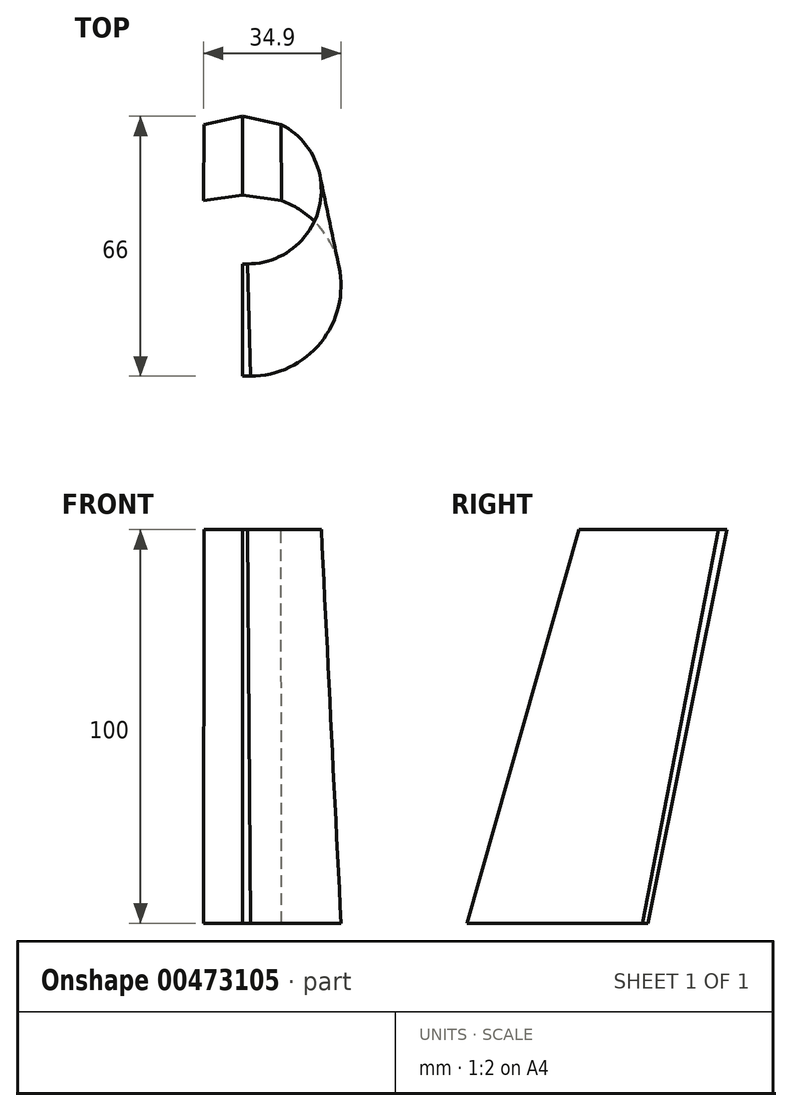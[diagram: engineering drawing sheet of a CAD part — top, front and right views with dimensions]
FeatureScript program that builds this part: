
annotation { "Feature Type Name" : "Feature", "Feature Type Description" : "" }
export const myFeature = defineFeature(function(context is Context, id is Id, definition is map)
    precondition{}
    {
        {
            var Q0;
            Q0=qCreatedBy(makeId("Top.planeOp"),FACE);
            var sketch = newSketch(context, id + "F0", { "sketchPlane" : qUnion([Q0])});
            skLineSegment(sketch, "E0.top", {"start": v(25, 0) * mm, "end": v(-25, 0) * mm, "construction": true});
            skLineSegment(sketch, "E1", {"start": v(0, 0) * mm, "end": v(9.9, -1.4) * mm});
            skLineSegment(sketch, "E2", {"start": v(0, -46) * mm, "end": v(25, -46) * mm, "construction": true});
            skLineSegment(sketch, "E3", {"start": v(25, -46) * mm, "end": v(25, 0) * mm, "construction": true});
            skArc(sketch, "E4", {"start": v(25, -46) * mm, "mid": v(2, -23) * mm, "end": v(25, 0) * mm, "construction": true});
            skLineSegment(sketch, "E5", {"start": v(0, 0) * mm, "end": v(0, -46) * mm, "construction": true});
            skLineSegment(sketch, "E6", {"start": v(2, -23) * mm, "end": v(2, -46) * mm, "construction": true});
            skArc(sketch, "E7", {"start": v(2, -46) * mm, "mid": v(24.65, -27.01) * mm, "end": v(9.9, -1.4) * mm});
            skLineSegment(sketch, "E8", {"start": v(0, -46) * mm, "end": v(2, -46) * mm});
            skLineSegment(sketch, "E9.MirrorCS", {"start": v(0, -46) * mm, "end": v(-25, -46) * mm, "construction": true});
            skLineSegment(sketch, "E10", {"start": v(-25, -46) * mm, "end": v(-17.5, -46) * mm, "construction": true});
            skLineSegment(sketch, "E11", {"start": v(-17.5, -46) * mm, "end": v(-17.5, -38.5) * mm, "construction": true});
            skArc(sketch, "E12", {"start": v(-17.5, -46) * mm, "mid": v(-22.8, -43.8) * mm, "end": v(-25, -38.5) * mm});
            skLineSegment(sketch, "E13", {"start": v(-17.5, -46) * mm, "end": v(0, -46) * mm});
            skLineSegment(sketch, "E14", {"start": v(-25, -15.9) * mm, "end": v(-15, -15.9) * mm, "construction": true});
            skArc(sketch, "E15", {"start": v(-25, -15.9) * mm, "mid": v(-23.66, -10.9) * mm, "end": v(-20, -7.23) * mm});
            skLineSegment(sketch, "E16", {"start": v(-9.9, -1.4) * mm, "end": v(-20, -7.23) * mm});
            skLineSegment(sketch, "E17.MirrorCS", {"start": v(0, 0) * mm, "end": v(-9.9, -1.4) * mm});
            skLineSegment(sketch, "E18", {"start": v(-25, -38.5) * mm, "end": v(-25, -15.9) * mm});
            skSolve(sketch);
        }
        {
            var Q0;
            Q0=qCreatedBy(makeId("Top.planeOp"),FACE);
            cPlane(context, id + "F1", {"entities" : qUnion([Q0]), "cplaneType" : CPlaneType.OFFSET, "offset" : 100 * mm, "width" : 150 * mm, "height" : 150 * mm});
        }
        {
            var Q0;
            Q0=qCreatedBy(id+"F1.planeOp",FACE);
            var sketch = newSketch(context, id + "F2", { "sketchPlane" : qUnion([Q0])});
            skLineSegment(sketch, "E19", {"start": v(0, 0) * mm, "end": v(0, 20) * mm, "construction": true});
            skLineSegment(sketch, "E20.top", {"start": v(20, 20) * mm, "end": v(-20, 20) * mm, "construction": true});
            skLineSegment(sketch, "E21", {"start": v(0, 20) * mm, "end": v(9.79, 17.94) * mm});
            skLineSegment(sketch, "E22", {"start": v(0, -17.5) * mm, "end": v(20, -17.5) * mm, "construction": true});
            skLineSegment(sketch, "E23", {"start": v(20, -17.5) * mm, "end": v(20, 20) * mm, "construction": true});
            skArc(sketch, "E24", {"start": v(20, -17.5) * mm, "mid": v(1.25, 1.25) * mm, "end": v(20, 20) * mm, "construction": true});
            skLineSegment(sketch, "E25", {"start": v(0, 20) * mm, "end": v(0, -17.5) * mm, "construction": true});
            skLineSegment(sketch, "E26", {"start": v(1.25, 1.25) * mm, "end": v(1.25, -17.5) * mm, "construction": true});
            skArc(sketch, "E27", {"start": v(1.25, -17.5) * mm, "mid": v(19.48, -3.14) * mm, "end": v(9.79, 17.94) * mm});
            skLineSegment(sketch, "E28", {"start": v(0, -17.5) * mm, "end": v(1.25, -17.5) * mm});
            skLineSegment(sketch, "E29.MirrorCS", {"start": v(0, -17.5) * mm, "end": v(-20, -17.5) * mm, "construction": true});
            skLineSegment(sketch, "E30", {"start": v(-20, -17.5) * mm, "end": v(-12.5, -17.5) * mm, "construction": true});
            skLineSegment(sketch, "E31", {"start": v(-12.5, -17.5) * mm, "end": v(-12.5, -10) * mm, "construction": true});
            skArc(sketch, "E32", {"start": v(-12.5, -17.5) * mm, "mid": v(-17.8, -15.3) * mm, "end": v(-20, -10) * mm});
            skLineSegment(sketch, "E33", {"start": v(-12.5, -17.5) * mm, "end": v(0, -17.5) * mm});
            skLineSegment(sketch, "E34", {"start": v(-20, 6.27) * mm, "end": v(-10, 6.27) * mm, "construction": true});
            skArc(sketch, "E35", {"start": v(-20, 6.27) * mm, "mid": v(-18.66, 11.27) * mm, "end": v(-15, 14.93) * mm});
            skLineSegment(sketch, "E36", {"start": v(-9.79, 17.94) * mm, "end": v(-15, 14.93) * mm});
            skLineSegment(sketch, "E37.MirrorCS", {"start": v(0, 20) * mm, "end": v(-9.79, 17.94) * mm});
            skLineSegment(sketch, "E38", {"start": v(-20, -10) * mm, "end": v(-20, 6.27) * mm});
            skSolve(sketch);
        }
        {
            var Q0;
            Q0=sQuery(id+"F0.wireOp",EDGE,"E7");
            var Q1;
            Q1=sQuery(id+"F2.wireOp",EDGE,"E27");
            loft(context, id + "F3", {"bodyType" : ToolBodyType.SURFACE, "wireProfilesArray" : [{ "wireProfileEntities" : qUnion([Q0]) }, { "wireProfileEntities" : qUnion([Q1]) }]});
        }
        {
            var Q0;
            Q0=sQuery(id+"F0.wireOp",EDGE,"E1");
            var Q1;
            Q1=sQuery(id+"F2.wireOp",EDGE,"E21");
            loft(context, id + "F4", {"bodyType" : ToolBodyType.SURFACE, "wireProfilesArray" : [{ "wireProfileEntities" : qUnion([Q0]) }, { "wireProfileEntities" : qUnion([Q1]) }]});
        }
        {
            var Q0;
            Q0=sQuery(id+"F0.wireOp",EDGE,"E17.MirrorCS");
            var Q1;
            Q1=sQuery(id+"F2.wireOp",EDGE,"E37.MirrorCS");
            loft(context, id + "F5", {"bodyType" : ToolBodyType.SURFACE, "wireProfilesArray" : [{ "wireProfileEntities" : qUnion([Q0]) }, { "wireProfileEntities" : qUnion([Q1]) }]});
        }
        {
            var Q0;
            Q0=sQuery(id+"F2.wireOp",EDGE,"E28");
            var Q1;
            Q1=sQuery(id+"F0.wireOp",EDGE,"E8");
            loft(context, id + "F6", {"bodyType" : ToolBodyType.SURFACE, "wireProfilesArray" : [{ "wireProfileEntities" : qUnion([Q0]) }, { "wireProfileEntities" : qUnion([Q1]) }]});
        }
    });
